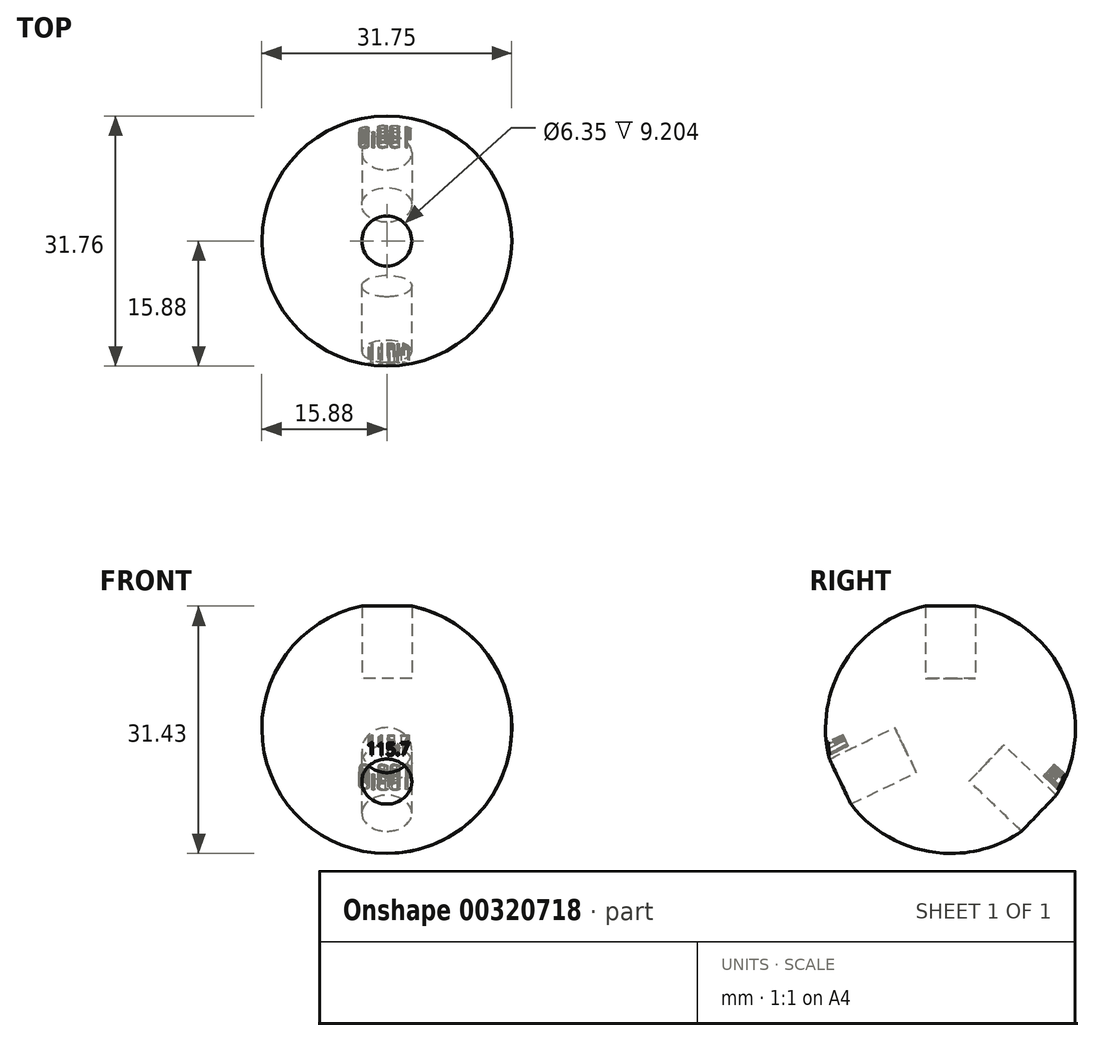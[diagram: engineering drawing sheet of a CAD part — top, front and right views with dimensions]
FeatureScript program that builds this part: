
annotation { "Feature Type Name" : "Feature", "Feature Type Description" : "" }
export const myFeature = defineFeature(function(context is Context, id is Id, definition is map)
    precondition{}
    {
        {
            var Q0;
            Q0=qCreatedBy(makeId("Front.planeOp"),FACE);
            var sketch = newSketch(context, id + "F0", { "sketchPlane" : qUnion([Q0])});
            skArc(sketch, "E0", {"start": v(0, 15.88) * mm, "mid": v(-15.88, 0) * mm, "end": v(0, -15.88) * mm});
            skLineSegment(sketch, "E1", {"start": v(0, 15.88) * mm, "end": v(0, -15.88) * mm});
            skSolve(sketch);
        }
        {
            var Q0;
            Q0=qCreatedBy(makeId("Top.planeOp"),FACE);
            var sketch = newSketch(context, id + "F1", { "sketchPlane" : qUnion([Q0])});
            skCircle(sketch, "E2", {"center": v(0, 0) * mm, "radius": 15.88 * mm});
            skSolve(sketch);
        }
        {
            var Q0;
            Q0=makeQuery(id+"F0.imprint","IMPRINT",FACE,{"disambiguationData":[TD([[makeQuery(id+"F0.imprint","IMPRINT",EDGE,{"derivedFrom":sQuery(id+"F0.wireOp",EDGE,"E0")}),1.0]])]});
            var Q1;
            Q1=sQuery(id+"F1.wireOp",EDGE,"E2");
            revolve(context, id + "F2", {"entities" : qUnion([Q0]), "axis" : qUnion([Q1]), "revolveType" : RevolveType.FULL});
        }
        {
            var Q0;
            Q0=qCreatedBy(makeId("Top.planeOp"),FACE);
            cPlane(context, id + "F3", {"entities" : qUnion([Q0]), "cplaneType" : CPlaneType.OFFSET, "offset" : 6.35 * mm, "width" : 152.4 * mm, "height" : 152.4 * mm});
        }
        {
            var Q0;
            Q0=qCreatedBy(id+"F3.planeOp",FACE);
            var sketch = newSketch(context, id + "F4", { "sketchPlane" : qUnion([Q0])});
            skCircle(sketch, "E3", {"center": v(0, 0) * mm, "radius": 3.17 * mm});
            skSolve(sketch);
        }
        {
            var Q0;
            Q0=makeQuery(id+"F4.imprint","IMPRINT",FACE,{"disambiguationData":[TD([[makeQuery(id+"F4.imprint","IMPRINT",EDGE,{"derivedFrom":sQuery(id+"F4.wireOp",EDGE,"E3")}),1.0]])]});
            extrude(context, id + "F5", {"entities" : qUnion([Q0]), "depth" : 50.8 * mm});
        }
        {
            var Q0;
            Q0=qCreatedBy(makeId("Front.planeOp"),FACE);
            var sketch = newSketch(context, id + "F6", { "sketchPlane" : qUnion([Q0])});
            skLineSegment(sketch, "E4", {"start": v(0, 0) * mm, "end": v(59.18, 0) * mm, "construction": true});
            skSolve(sketch);
        }
        {
            var Q0;
            Q0=makeQuery(id+"F5.opExtrude","SWEPT_BODY",BODY,{"disambiguationData":[OSD([sQuery(id+"F4.wireOp",EDGE,"E3")])]});
            var Q1;
            Q1=sQuery(id+"F6.wireOp",EDGE,"E4");
            transform(context, id + "F7", {"entities" : qUnion([Q0]), "transformType" : TransformType.ROTATION, "transformAxis" : qUnion([Q1]), "angle" : 115.7 * degree, "makeCopy" : true});
        }
        {
            var Q0;
            Q0=makeQuery(id+"F5.opExtrude","SWEPT_BODY",BODY,{"disambiguationData":[OSD([sQuery(id+"F4.wireOp",EDGE,"E3")])]});
            var Q1;
            Q1=sQuery(id+"F6.wireOp",EDGE,"E4");
            transform(context, id + "F8", {"entities" : qUnion([Q0]), "transformType" : TransformType.ROTATION, "transformAxis" : qUnion([Q1]), "angle" : 133.8 * degree, "oppositeDirection" : true, "makeCopy" : true});
        }
        {
            var Q0;
            Q0=makeQuery(id+"F7.opPattern","COPY",FACE,{"derivedFrom":makeQuery(id+"F5.opExtrude","CAP_FACE",FACE,{"disambiguationData":[OSD([sQuery(id+"F4.wireOp",EDGE,"E3")])],"isStart":false}),"instanceName":"1"});
            cPlane(context, id + "F9", {"entities" : qUnion([Q0]), "cplaneType" : CPlaneType.OFFSET, "offset" : 38.1 * mm, "oppositeDirection" : true, "width" : 152.4 * mm, "height" : 152.4 * mm});
        }
        {
            var Q0;
            Q0=qCreatedBy(id+"F9.planeOp",FACE);
            var sketch = newSketch(context, id + "F10", { "sketchPlane" : qUnion([Q0])});
            skText(sketch, "E5", { "text": "115.7\n", "fontName": "OpenSans-Regular.ttf"});
            const initialGuessF10  = {"E5": [-0.00255, 0.00366, 1, 0, 0.00154]};
            skSetInitialGuess(sketch, initialGuessF10);
            skSolve(sketch);
        }
        {
            var Q0;
            Q0=qSketchRegion(id+"F10",true);
            extrude(context, id + "F11", {"entities" : qUnion([Q0]), "operationType" : NewBodyOperationType.REMOVE, "oppositeDirection" : true, "depth" : 6.35 * mm});
        }
        {
            var Q0;
            Q0=makeQuery(id+"F8.opPattern","COPY",FACE,{"derivedFrom":makeQuery(id+"F5.opExtrude","CAP_FACE",FACE,{"disambiguationData":[OSD([sQuery(id+"F4.wireOp",EDGE,"E3")])],"isStart":false}),"instanceName":"1"});
            cPlane(context, id + "F12", {"entities" : qUnion([Q0]), "cplaneType" : CPlaneType.OFFSET, "offset" : 38.1 * mm, "oppositeDirection" : true, "width" : 152.4 * mm, "height" : 152.4 * mm});
        }
        {
            var Q0;
            Q0=qCreatedBy(id+"F12.planeOp",FACE);
            var sketch = newSketch(context, id + "F13", { "sketchPlane" : qUnion([Q0])});
            skText(sketch, "E6", { "text": "133.8\n", "fontName": "OpenSans-Regular.ttf"});
            const initialGuessF13  = {"E6": [-0.00335, 0.00387, 1, 0, 0.00198]};
            skSetInitialGuess(sketch, initialGuessF13);
            skSolve(sketch);
        }
        {
            var Q0;
            Q0=qSketchRegion(id+"F13",true);
            extrude(context, id + "F14", {"entities" : qUnion([Q0]), "operationType" : NewBodyOperationType.REMOVE, "oppositeDirection" : true, "depth" : 6.35 * mm});
        }
        {
            var Q0;
            Q0=makeQuery(id+"F5.opExtrude","SWEPT_BODY",BODY,{"disambiguationData":[OSD([sQuery(id+"F4.wireOp",EDGE,"E3")])]});
            var Q1;
            Q1=makeQuery(id+"F7.opPattern","COPY",BODY,{"derivedFrom":makeQuery(id+"F5.opExtrude","SWEPT_BODY",BODY,{"disambiguationData":[OSD([sQuery(id+"F4.wireOp",EDGE,"E3")])]}),"instanceName":"1"});
            var Q2;
            Q2=makeQuery(id+"F8.opPattern","COPY",BODY,{"derivedFrom":makeQuery(id+"F5.opExtrude","SWEPT_BODY",BODY,{"disambiguationData":[OSD([sQuery(id+"F4.wireOp",EDGE,"E3")])]}),"instanceName":"1"});
            var Q3;
            Q3=makeQuery(id+"F2.opRevolve","SWEPT_BODY",BODY,{"disambiguationData":[OSD([sQuery(id+"F0.wireOp",EDGE,"E0"),sQuery(id+"F0.wireOp",EDGE,"E1")])]});
            booleanBodies(context, id + "F15", {"operationType" : BooleanOperationType.SUBTRACTION, "tools" : qUnion([Q0, Q1, Q2]), "targets" : qUnion([Q3])});
        }
    });
